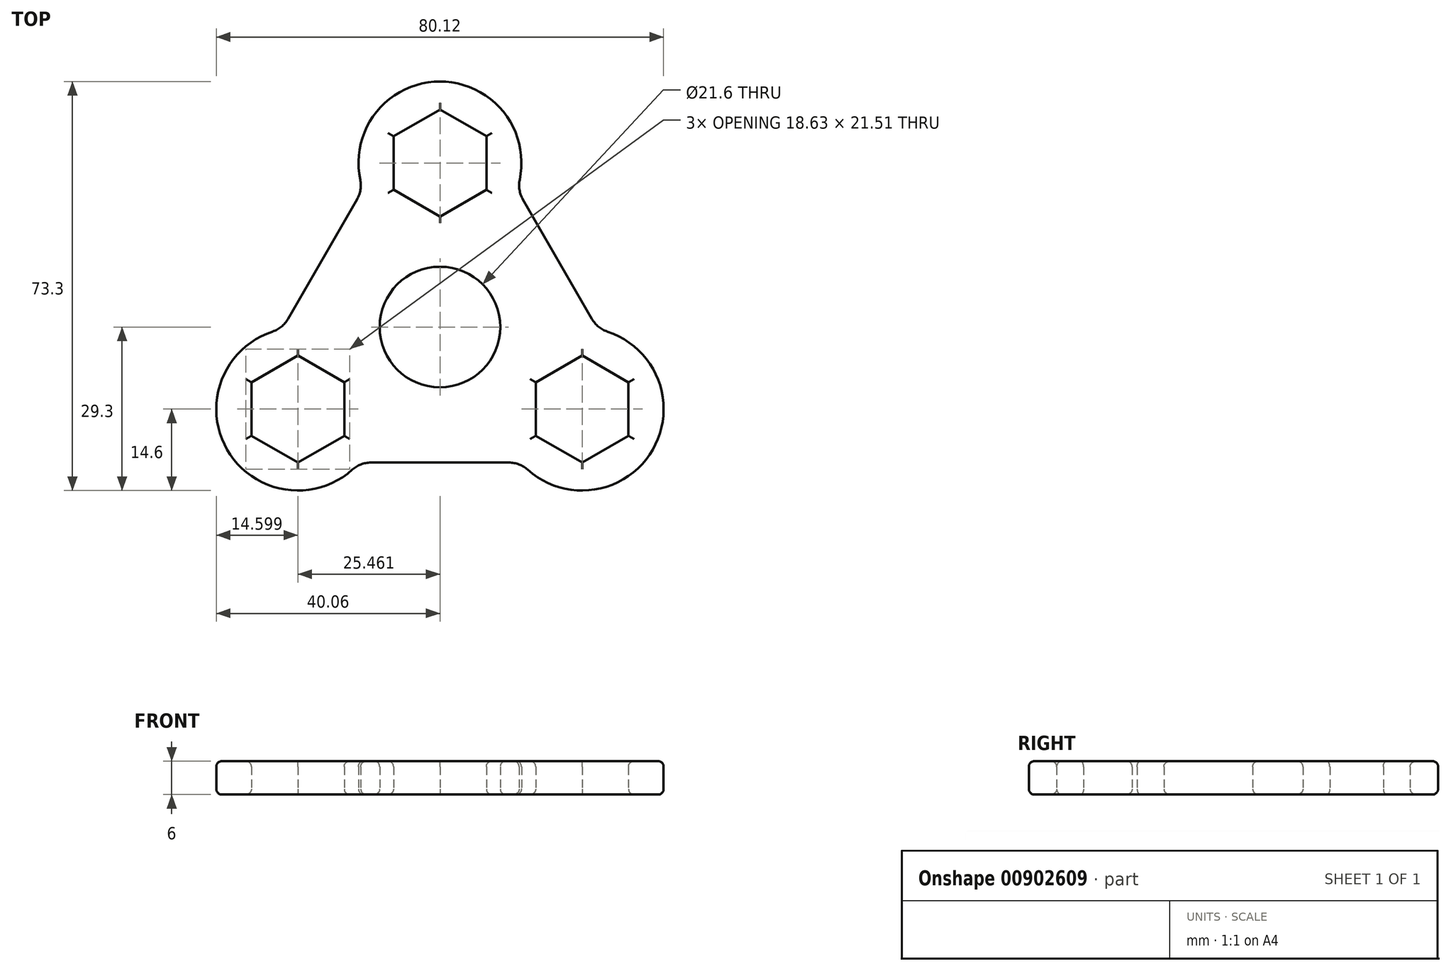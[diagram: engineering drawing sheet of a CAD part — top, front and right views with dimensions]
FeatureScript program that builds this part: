
annotation { "Feature Type Name" : "Feature", "Feature Type Description" : "" }
export const myFeature = defineFeature(function(context is Context, id is Id, definition is map)
    precondition{}
    {
        {
            var Q0;
            Q0=qCreatedBy(makeId("Top.planeOp"),FACE);
            var sketch = newSketch(context, id + "F0", { "sketchPlane" : qUnion([Q0])});
            skCircle(sketch, "E0", {"center": v(0, 0) * mm, "radius": 10.8 * mm});
            skLineSegment(sketch, "E1", {"start": v(0, 0) * mm, "end": v(0, 44) * mm, "construction": true});
            skCircle(sketch, "E2.cCircle", {"center": v(0, 29.4) * mm, "radius": 8.31 * mm, "construction": true});
            skLineSegment(sketch, "E2.0", {"start": v(8.31, 34.2) * mm, "end": v(8.31, 24.6) * mm});
            skLineSegment(sketch, "E2.1", {"start": v(8.31, 24.6) * mm, "end": v(0, 19.8) * mm});
            skLineSegment(sketch, "E2.2", {"start": v(0, 19.8) * mm, "end": v(-8.31, 24.6) * mm});
            skLineSegment(sketch, "E2.3", {"start": v(-8.31, 24.6) * mm, "end": v(-8.31, 34.2) * mm});
            skLineSegment(sketch, "E2.4", {"start": v(-8.31, 34.2) * mm, "end": v(0, 39) * mm});
            skLineSegment(sketch, "E2.5", {"start": v(0, 39) * mm, "end": v(8.31, 34.2) * mm});
            skPoint(sketch, "E2.0.midPoint", {"position": v(8.31, 29.4) * mm});
            skArc(sketch, "E3", {"start": v(14.29, 26.4) * mm, "mid": v(0, 44) * mm, "end": v(-14.29, 26.4) * mm});
            skLineSegment(sketch, "E4.1.0", {"start": v(-25.46, -5.1) * mm, "end": v(-17.15, -9.9) * mm});
            skLineSegment(sketch, "E4.1.1", {"start": v(-17.15, -9.9) * mm, "end": v(-17.15, -19.5) * mm});
            skLineSegment(sketch, "E4.1.2", {"start": v(-25.46, -24.3) * mm, "end": v(-33.77, -19.5) * mm});
            skCircle(sketch, "E4.1.3", {"center": v(-25.46, -14.7) * mm, "radius": 8.31 * mm, "construction": true});
            skPoint(sketch, "E4.1.4", {"position": v(-29.62, -7.5) * mm});
            skArc(sketch, "E4.1.5", {"start": v(-30, -0.83) * mm, "mid": v(-38.1, -22) * mm, "end": v(-15.72, -25.58) * mm});
            skLineSegment(sketch, "E4.1.6", {"start": v(-33.77, -19.5) * mm, "end": v(-33.77, -9.9) * mm});
            skLineSegment(sketch, "E4.1.7", {"start": v(-17.15, -19.5) * mm, "end": v(-25.46, -24.3) * mm});
            skLineSegment(sketch, "E4.1.8", {"start": v(-33.77, -9.9) * mm, "end": v(-25.46, -5.1) * mm});
            skLineSegment(sketch, "E4.2.0", {"start": v(17.15, -19.5) * mm, "end": v(17.15, -9.9) * mm});
            skLineSegment(sketch, "E4.2.1", {"start": v(17.15, -9.9) * mm, "end": v(25.46, -5.1) * mm});
            skLineSegment(sketch, "E4.2.2", {"start": v(33.77, -9.9) * mm, "end": v(33.77, -19.5) * mm});
            skCircle(sketch, "E4.2.3", {"center": v(25.46, -14.7) * mm, "radius": 8.31 * mm, "construction": true});
            skPoint(sketch, "E4.2.4", {"position": v(21.3, -21.9) * mm});
            skArc(sketch, "E4.2.5", {"start": v(15.72, -25.58) * mm, "mid": v(38.1, -22) * mm, "end": v(30, -0.83) * mm});
            skLineSegment(sketch, "E4.2.6", {"start": v(33.77, -19.5) * mm, "end": v(25.46, -24.3) * mm});
            skLineSegment(sketch, "E4.2.7", {"start": v(25.46, -5.1) * mm, "end": v(33.77, -9.9) * mm});
            skLineSegment(sketch, "E4.2.8", {"start": v(25.46, -24.3) * mm, "end": v(17.15, -19.5) * mm});
            skLineSegment(sketch, "E5", {"start": v(-14.85, 22.88) * mm, "end": v(-27.24, 1.42) * mm});
            skLineSegment(sketch, "E6", {"start": v(-12.38, -24.3) * mm, "end": v(12.38, -24.3) * mm});
            skLineSegment(sketch, "E7", {"start": v(27.24, 1.42) * mm, "end": v(14.85, 22.88) * mm});
            skPoint(sketch, "E8.visualSharp", {"position": v(-13.81, 24.67) * mm});
            skArc(sketch, "E8.filletArc", {"start": v(-14.85, 22.88) * mm, "mid": v(-14.24, 24.59) * mm, "end": v(-14.29, 26.4) * mm});
            skPoint(sketch, "E9.visualSharp", {"position": v(13.81, 24.67) * mm});
            skArc(sketch, "E9.filletArc", {"start": v(14.29, 26.4) * mm, "mid": v(14.24, 24.59) * mm, "end": v(14.85, 22.88) * mm});
            skPoint(sketch, "E10.visualSharp", {"position": v(28.27, -0.37) * mm});
            skArc(sketch, "E10.filletArc", {"start": v(27.24, 1.42) * mm, "mid": v(28.42, 0.04) * mm, "end": v(30, -0.83) * mm});
            skPoint(sketch, "E11.visualSharp", {"position": v(14.46, -24.3) * mm});
            skArc(sketch, "E11.filletArc", {"start": v(15.72, -25.58) * mm, "mid": v(14.17, -24.63) * mm, "end": v(12.38, -24.3) * mm});
            skPoint(sketch, "E12.visualSharp", {"position": v(-14.46, -24.3) * mm});
            skArc(sketch, "E12.filletArc", {"start": v(-12.38, -24.3) * mm, "mid": v(-14.17, -24.63) * mm, "end": v(-15.72, -25.58) * mm});
            skPoint(sketch, "E13.visualSharp", {"position": v(-28.27, -0.37) * mm});
            skArc(sketch, "E13.filletArc", {"start": v(-30, -0.83) * mm, "mid": v(-28.42, 0.04) * mm, "end": v(-27.24, 1.42) * mm});
            skSolve(sketch);
        }
        {
            var Q0;
            Q0=makeQuery(id+"F0.imprint","IMPRINT",FACE,{"disambiguationData":[TD([[makeQuery(id+"F0.imprint","IMPRINT",EDGE,{"derivedFrom":sQuery(id+"F0.wireOp",EDGE,"E0")}),-1.0]])]});
            extrude(context, id + "F1", {"entities" : qUnion([Q0]), "depth" : 6 * mm, "offsetDistance" : 25 * mm});
        }
        {
            var Q0;
            Q0=makeQuery(id+"F1.opExtrude","CAP_FACE",FACE,{"disambiguationData":[OSD([sQuery(id+"F0.wireOp",EDGE,"E0"),sQuery(id+"F0.wireOp",EDGE,"E2.0"),sQuery(id+"F0.wireOp",EDGE,"E2.1"),sQuery(id+"F0.wireOp",EDGE,"E2.2"),sQuery(id+"F0.wireOp",EDGE,"E2.3"),sQuery(id+"F0.wireOp",EDGE,"E2.4"),sQuery(id+"F0.wireOp",EDGE,"E2.5"),sQuery(id+"F0.wireOp",EDGE,"E3"),sQuery(id+"F0.wireOp",EDGE,"E4.1.0"),sQuery(id+"F0.wireOp",EDGE,"E4.1.1"),sQuery(id+"F0.wireOp",EDGE,"E4.1.2"),sQuery(id+"F0.wireOp",EDGE,"E4.1.5"),sQuery(id+"F0.wireOp",EDGE,"E4.1.6"),sQuery(id+"F0.wireOp",EDGE,"E4.1.7"),sQuery(id+"F0.wireOp",EDGE,"E4.1.8"),sQuery(id+"F0.wireOp",EDGE,"E4.2.0"),sQuery(id+"F0.wireOp",EDGE,"E4.2.1"),sQuery(id+"F0.wireOp",EDGE,"E4.2.2"),sQuery(id+"F0.wireOp",EDGE,"E4.2.5"),sQuery(id+"F0.wireOp",EDGE,"E4.2.6"),sQuery(id+"F0.wireOp",EDGE,"E4.2.7"),sQuery(id+"F0.wireOp",EDGE,"E4.2.8"),sQuery(id+"F0.wireOp",EDGE,"E5"),sQuery(id+"F0.wireOp",EDGE,"E6"),sQuery(id+"F0.wireOp",EDGE,"E7"),sQuery(id+"F0.wireOp",EDGE,"E8.filletArc"),sQuery(id+"F0.wireOp",EDGE,"E9.filletArc"),sQuery(id+"F0.wireOp",EDGE,"E10.filletArc"),sQuery(id+"F0.wireOp",EDGE,"E11.filletArc"),sQuery(id+"F0.wireOp",EDGE,"E12.filletArc"),sQuery(id+"F0.wireOp",EDGE,"E13.filletArc")])],"isStart":false});
            var Q1;
            Q1=makeQuery(id+"F1.opExtrude","CAP_EDGE",EDGE,{"disambiguationData":[OSD([sQuery(id+"F0.wireOp",EDGE,"E5")])],"isStart":true});
            var Q2;
            Q2=makeQuery(id+"F1.opExtrude","CAP_FACE",FACE,{"disambiguationData":[OSD([sQuery(id+"F0.wireOp",EDGE,"E0"),sQuery(id+"F0.wireOp",EDGE,"E2.0"),sQuery(id+"F0.wireOp",EDGE,"E2.1"),sQuery(id+"F0.wireOp",EDGE,"E2.2"),sQuery(id+"F0.wireOp",EDGE,"E2.3"),sQuery(id+"F0.wireOp",EDGE,"E2.4"),sQuery(id+"F0.wireOp",EDGE,"E2.5"),sQuery(id+"F0.wireOp",EDGE,"E3"),sQuery(id+"F0.wireOp",EDGE,"E4.1.0"),sQuery(id+"F0.wireOp",EDGE,"E4.1.1"),sQuery(id+"F0.wireOp",EDGE,"E4.1.2"),sQuery(id+"F0.wireOp",EDGE,"E4.1.5"),sQuery(id+"F0.wireOp",EDGE,"E4.1.6"),sQuery(id+"F0.wireOp",EDGE,"E4.1.7"),sQuery(id+"F0.wireOp",EDGE,"E4.1.8"),sQuery(id+"F0.wireOp",EDGE,"E4.2.0"),sQuery(id+"F0.wireOp",EDGE,"E4.2.1"),sQuery(id+"F0.wireOp",EDGE,"E4.2.2"),sQuery(id+"F0.wireOp",EDGE,"E4.2.5"),sQuery(id+"F0.wireOp",EDGE,"E4.2.6"),sQuery(id+"F0.wireOp",EDGE,"E4.2.7"),sQuery(id+"F0.wireOp",EDGE,"E4.2.8"),sQuery(id+"F0.wireOp",EDGE,"E5"),sQuery(id+"F0.wireOp",EDGE,"E6"),sQuery(id+"F0.wireOp",EDGE,"E7"),sQuery(id+"F0.wireOp",EDGE,"E8.filletArc"),sQuery(id+"F0.wireOp",EDGE,"E9.filletArc"),sQuery(id+"F0.wireOp",EDGE,"E10.filletArc"),sQuery(id+"F0.wireOp",EDGE,"E11.filletArc"),sQuery(id+"F0.wireOp",EDGE,"E12.filletArc"),sQuery(id+"F0.wireOp",EDGE,"E13.filletArc")])],"isStart":true});
            fillet(context, id + "F2", {"entities" : qUnion([Q0, Q1, Q2]), "radius" : 1 * mm, "tangentPropagation" : true, "allowEdgeOverflow" : false});
        }
    });
